# Revit family: QF_BOURGEAT_plaque_chauffante_extra_basse
name_source: partatom
category: Equipement spécialisé
revit_build: Autodesk Revit 2015 (Build: 20140606_1530(x64)
units: mm (PartAtom-declared; Revit-internal decimal feet)

## types (2) — shared parameters
Charge max = 10.00 kg
Fabricant = BOURGEAT
Fréquence = 50 Hz
Indice de protection = 21
Intensité nominale = 1 A
Phase = 2
Spécification du Fabricant = PLAQUE CHAUFFANTE
Tension = 230 V
URL catalogue = http://www.bourgeat.fr

## per-type parameters (varying)
| type | Hauteur hors tout | Longueur hors tout | Modèle | Poids net à vide | Profondeur hors tout | Puissance électrique  |
| GN1/1 | 38 mm  [stored 0.124672 ft] | 530 mm  [stored 1.73885 ft] | 870801 | 2.00 kg | 325 mm  [stored 1.06627 ft] | 225 W |
| 400x600 | 42 mm  [stored 0.137795 ft] | 600 mm | 870804 | 2.50 kg | 400 mm  [stored 1.31234 ft] | 300 W |

note: [stored X ft] marks values corroborated as IEEE doubles in the binary element streams (Revit-internal decimal feet)
